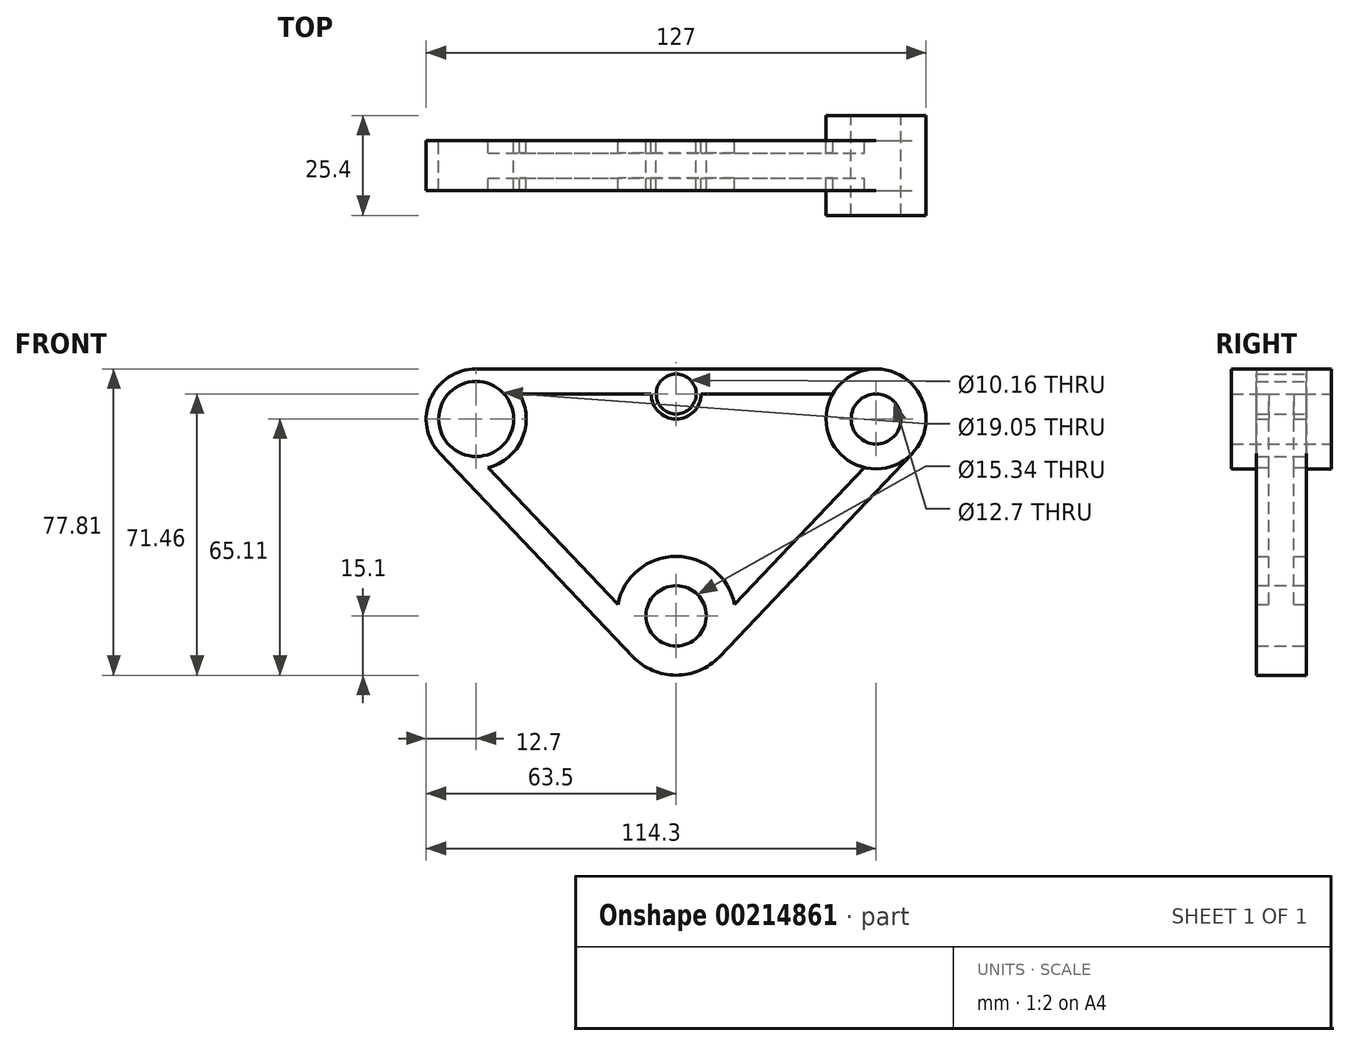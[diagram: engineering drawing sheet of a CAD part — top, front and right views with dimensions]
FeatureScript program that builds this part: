
annotation { "Feature Type Name" : "Feature", "Feature Type Description" : "" }
export const myFeature = defineFeature(function(context is Context, id is Id, definition is map)
    precondition{}
    {
        {
            var Q0;
            Q0=qCreatedBy(makeId("Front.planeOp"),FACE);
            var sketch = newSketch(context, id + "F0", { "sketchPlane" : qUnion([Q0])});
            skCircle(sketch, "E0", {"center": v(-50.8, 24.6) * mm, "radius": 12.7 * mm});
            skCircle(sketch, "E1", {"center": v(0, 30.96) * mm, "radius": 6.35 * mm});
            skCircle(sketch, "E2", {"center": v(50.8, 24.6) * mm, "radius": 12.7 * mm});
            skCircle(sketch, "E3", {"center": v(0, -25.4) * mm, "radius": 15.1 * mm});
            skLineSegment(sketch, "E4", {"start": v(-60, 15.86) * mm, "end": v(-10.95, -35.8) * mm});
            skLineSegment(sketch, "E5", {"start": v(-50.8, 37.3) * mm, "end": v(0, 37.3) * mm});
            skLineSegment(sketch, "E6", {"start": v(0, 37.3) * mm, "end": v(50.8, 37.3) * mm});
            skLineSegment(sketch, "E7", {"start": v(10.95, -35.8) * mm, "end": v(60, 15.86) * mm});
            skCircle(sketch, "E8", {"center": v(-50.8, 24.6) * mm, "radius": 9.53 * mm});
            skCircle(sketch, "E9", {"center": v(0, 30.96) * mm, "radius": 5.08 * mm});
            skCircle(sketch, "E10", {"center": v(50.8, 24.6) * mm, "radius": 6.35 * mm});
            skCircle(sketch, "E11", {"center": v(0, -25.4) * mm, "radius": 7.67 * mm});
            skLineSegment(sketch, "E12.0", {"start": v(6.35, 30.96) * mm, "end": v(39.8, 30.96) * mm});
            skLineSegment(sketch, "E13.0", {"start": v(14.82, -22.5) * mm, "end": v(47.83, 12.26) * mm});
            skLineSegment(sketch, "E14.0", {"start": v(-47.83, 12.26) * mm, "end": v(-14.82, -22.5) * mm});
            skLineSegment(sketch, "E15.trimOffspring", {"start": v(-39.8, 30.96) * mm, "end": v(-6.35, 30.96) * mm});
            skSolve(sketch);
        }
        {
            var Q0;
            Q0=makeQuery(id+"F0.imprint","IMPRINT",FACE,{"disambiguationData":[TD([[makeQuery(id+"F0.imprint","IMPRINT",EDGE,{"derivedFrom":sQuery(id+"F0.wireOp",EDGE,"E8")}),-1.0]])]});
            var Q1;
            {var subQ0=sQuery(id+"F0.wireOp",EDGE,"E5");Q1=makeQuery(id+"F0.imprint","IMPRINT",FACE,{"disambiguationData":[TD([[makeQuery(id+"F0.imprint","IMPRINT",EDGE,{"derivedFrom":subQ0}),-1.0]])]});}
            var Q2;
            Q2=makeQuery(id+"F0.imprint","IMPRINT",FACE,{"disambiguationData":[TD([[makeQuery(id+"F0.imprint","IMPRINT",EDGE,{"derivedFrom":sQuery(id+"F0.wireOp",EDGE,"E9")}),-1.0]])]});
            var Q3;
            {var subQ0=sQuery(id+"F0.wireOp",EDGE,"E6");Q3=makeQuery(id+"F0.imprint","IMPRINT",FACE,{"disambiguationData":[TD([[makeQuery(id+"F0.imprint","IMPRINT",EDGE,{"derivedFrom":subQ0}),-1.0]])]});}
            var Q4;
            Q4=makeQuery(id+"F0.imprint","IMPRINT",FACE,{"disambiguationData":[TD([[makeQuery(id+"F0.imprint","IMPRINT",EDGE,{"derivedFrom":sQuery(id+"F0.wireOp",EDGE,"E10")}),-1.0]])]});
            var Q5;
            {var subQ0=sQuery(id+"F0.wireOp",EDGE,"E7");Q5=makeQuery(id+"F0.imprint","IMPRINT",FACE,{"disambiguationData":[TD([[makeQuery(id+"F0.imprint","IMPRINT",EDGE,{"derivedFrom":subQ0}),1.0]])]});}
            var Q6;
            Q6=makeQuery(id+"F0.imprint","IMPRINT",FACE,{"disambiguationData":[TD([[makeQuery(id+"F0.imprint","IMPRINT",EDGE,{"derivedFrom":sQuery(id+"F0.wireOp",EDGE,"E11")}),-1.0]])]});
            var Q7;
            {var subQ0=sQuery(id+"F0.wireOp",EDGE,"E4");Q7=makeQuery(id+"F0.imprint","IMPRINT",FACE,{"disambiguationData":[TD([[makeQuery(id+"F0.imprint","IMPRINT",EDGE,{"derivedFrom":subQ0}),1.0]])]});}
            extrude(context, id + "F1", {"entities" : qUnion([Q0, Q1, Q2, Q3, Q4, Q5, Q6, Q7]), "endBound" : BoundingType.SYMMETRIC, "depth" : 12.7 * mm});
        }
        {
            var Q0;
            {var subQ3=sQuery(id+"F0.wireOp",EDGE,"E12.0");Q0=makeQuery(id+"F0.imprint","IMPRINT",FACE,{"disambiguationData":[TD([[makeQuery(id+"F0.imprint","IMPRINT",EDGE,{"derivedFrom":subQ3}),-1.0]])]});}
            extrude(context, id + "F2", {"entities" : qUnion([Q0]), "operationType" : NewBodyOperationType.ADD, "endBound" : BoundingType.SYMMETRIC, "depth" : 6.35 * mm});
        }
        {
            var Q0;
            Q0=makeQuery(id+"F0.imprint","IMPRINT",FACE,{"disambiguationData":[TD([[makeQuery(id+"F0.imprint","IMPRINT",EDGE,{"derivedFrom":sQuery(id+"F0.wireOp",EDGE,"E10")}),-1.0]])]});
            extrude(context, id + "F3", {"entities" : qUnion([Q0]), "operationType" : NewBodyOperationType.ADD, "endBound" : BoundingType.SYMMETRIC, "depth" : 25.4 * mm});
        }
    });
